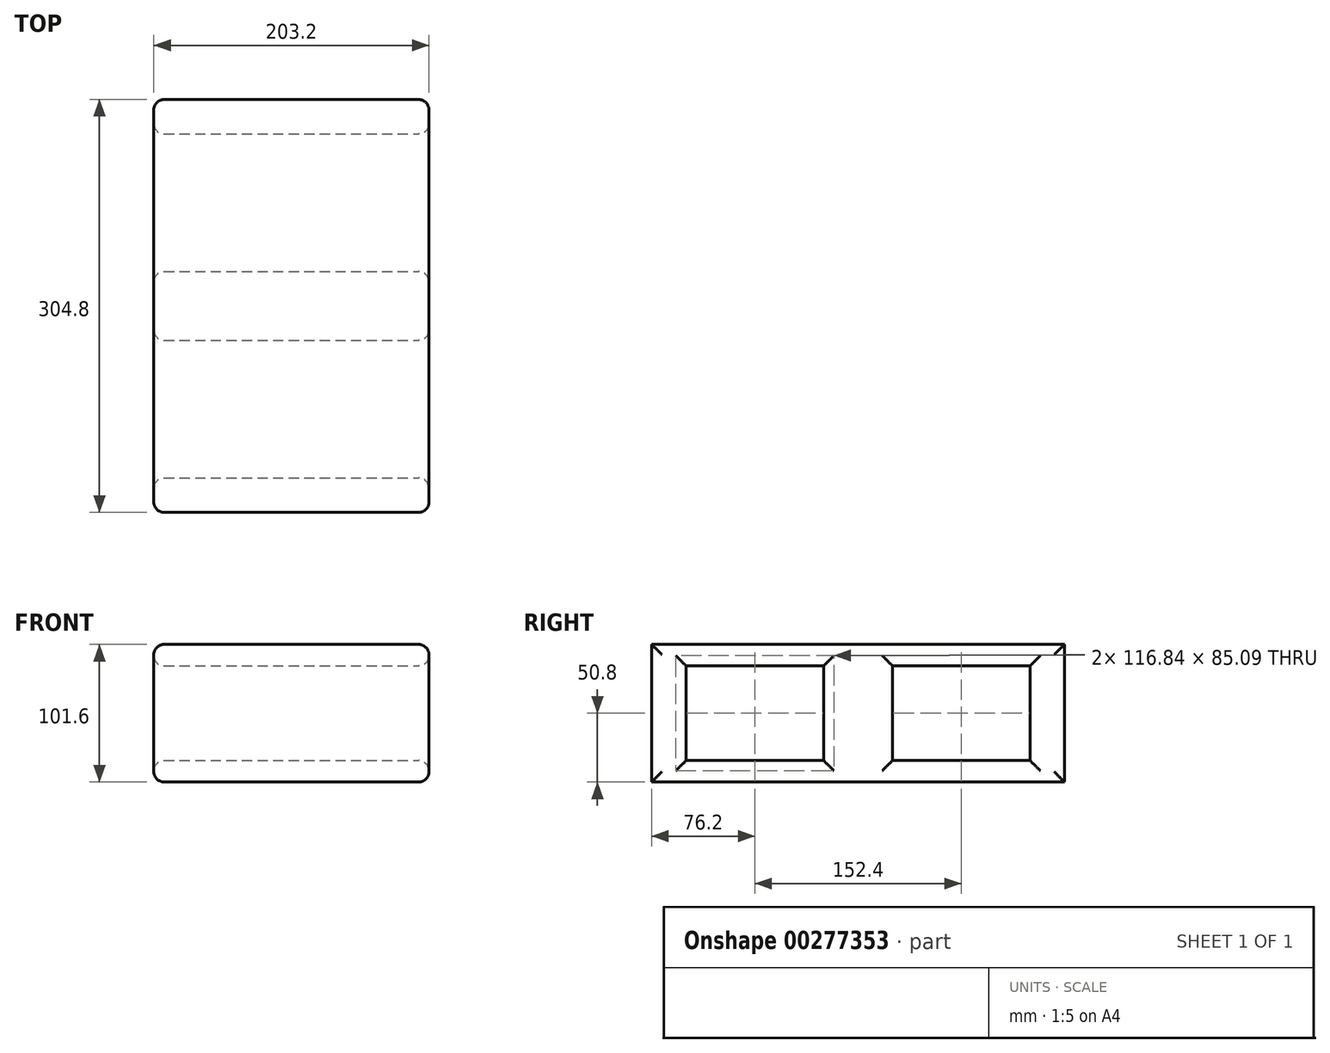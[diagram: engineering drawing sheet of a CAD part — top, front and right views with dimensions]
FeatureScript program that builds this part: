
annotation { "Feature Type Name" : "Feature", "Feature Type Description" : "" }
export const myFeature = defineFeature(function(context is Context, id is Id, definition is map)
    precondition{}
    {
        {
            var Q0;
            Q0=qCreatedBy(makeId("Front.planeOp"),FACE);
            var sketch = newSketch(context, id + "F0", { "sketchPlane" : qUnion([Q0])});
            skLineSegment(sketch, "E0.bottom", {"start": v(101.6, 50.8) * mm, "end": v(-101.6, 50.8) * mm});
            skLineSegment(sketch, "E0.top", {"start": v(101.6, -50.8) * mm, "end": v(-101.6, -50.8) * mm});
            skLineSegment(sketch, "E0.left", {"start": v(101.6, 50.8) * mm, "end": v(101.6, -50.8) * mm});
            skLineSegment(sketch, "E0.right", {"start": v(-101.6, 50.8) * mm, "end": v(-101.6, -50.8) * mm});
            skPoint(sketch, "E0.middle", {"position": v(0, 0) * mm});
            skSolve(sketch);
        }
        {
            var Q0;
            Q0 = qSketchRegion(id + "F0", true);
            extrude(context, id + "F1", {"entities" : qUnion([Q0]), "depth" : 304.8 * mm});
        }
        {
            var Q0;
            Q0=makeQuery(id+"F1.opExtrude","SWEPT_FACE",FACE,{"disambiguationData":[OSD([sQuery(id+"F0.wireOp",EDGE,"E0.left")])]});
            var sketch = newSketch(context, id + "F2", { "sketchPlane" : qUnion([Q0])});
            skLineSegment(sketch, "E1", {"start": v(-304.8, 0) * mm, "end": v(0, 0) * mm, "construction": true});
            skLineSegment(sketch, "E2.bottom", {"start": v(-177.8, 34.93) * mm, "end": v(-279.4, 34.93) * mm});
            skLineSegment(sketch, "E2.top", {"start": v(-177.8, -34.92) * mm, "end": v(-279.4, -34.92) * mm});
            skLineSegment(sketch, "E2.left", {"start": v(-177.8, 34.93) * mm, "end": v(-177.8, -34.93) * mm});
            skLineSegment(sketch, "E2.right", {"start": v(-279.4, 34.93) * mm, "end": v(-279.4, -34.92) * mm});
            skPoint(sketch, "E2.middle", {"position": v(-228.6, 0) * mm});
            skLineSegment(sketch, "E3.bottom", {"start": v(-25.4, 34.92) * mm, "end": v(-127, 34.92) * mm});
            skLineSegment(sketch, "E3.top", {"start": v(-25.4, -34.92) * mm, "end": v(-127, -34.92) * mm});
            skLineSegment(sketch, "E3.left", {"start": v(-25.4, 34.92) * mm, "end": v(-25.4, -34.92) * mm});
            skLineSegment(sketch, "E3.right", {"start": v(-127, 34.92) * mm, "end": v(-127, -34.92) * mm});
            skPoint(sketch, "E3.middle", {"position": v(-76.2, 0) * mm});
            skSolve(sketch);
        }
        {
            var Q0;
            Q0 = qSketchRegion(id + "F2", true);
            extrude(context, id + "F3", {"entities" : qUnion([Q0]), "operationType" : NewBodyOperationType.REMOVE, "endBound" : BoundingType.THROUGH_ALL, "oppositeDirection" : true, "depth" : 25.4 * mm});
        }
        {
            var Q0;
            Q0=makeQuery(id+"F1.opExtrude","SWEPT_FACE",FACE,{"disambiguationData":[OSD([sQuery(id+"F0.wireOp",EDGE,"E0.right")])]});
            var Q1;
            Q1=makeQuery(id+"F1.opExtrude","SWEPT_FACE",FACE,{"disambiguationData":[OSD([sQuery(id+"F0.wireOp",EDGE,"E0.left")])]});
            fillet(context, id + "F4", {"entities" : qUnion([Q0, Q1]), "radius" : 7.62 * mm, "tangentPropagation" : true, "allowEdgeOverflow" : false});
        }
    });
